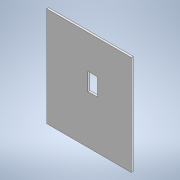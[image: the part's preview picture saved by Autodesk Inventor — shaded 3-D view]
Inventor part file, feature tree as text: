
AUTODESK INVENTOR PART (.ipt)
format: ipt  version: 2022.3 (Build 263350000, 350)  size: 113,664 bytes
history: native  units: mm
features: reference x6, other x4, extrude x3, sketch x3, projected_geometry x1
ambient origin geometry x8: Origin, YZ Plane, XZ Plane, XY Plane, X Axis, Y Axis, Z Axis, Center Point
bodies: Solid1 (feature_tree)
feature tree (17):
  extrude  "Extrusion1"  Depth=0.2mm TaperAngle=0.0deg
  extrude  "Extrusion2"  [1 undecoded]
  extrude  "Extrusion3"  [1 undecoded]
  sketch  "Sketch1"  dims[d0=0.7mm d1=0.0mm d2=0.2mm d3=0.0mm]
  reference  "Reference1"
  reference  "Reference2"
  reference  "Reference3"
  reference  "Reference4"
  reference  "Reference5"
  sketch  "Sketch2"  dims[d4=0.0mm d5=0.0mm]
  projected_geometry  "Projected Loop1"
  sketch  "Sketch3"
  reference  "Reference6"
  other  "<userpath>\Documents\Inventor\NanoSumo\Przekładnia.iam"
  other  "Przekładnia.iam"
  other  "TOF_VL53L0X (1):1"
  other  "pcb:1"
note: 2 required parameter values undecoded (feature->parameter linkage not recoverable at this tier; creation-order binding heuristic only, values carry confidence <= 0.55)
